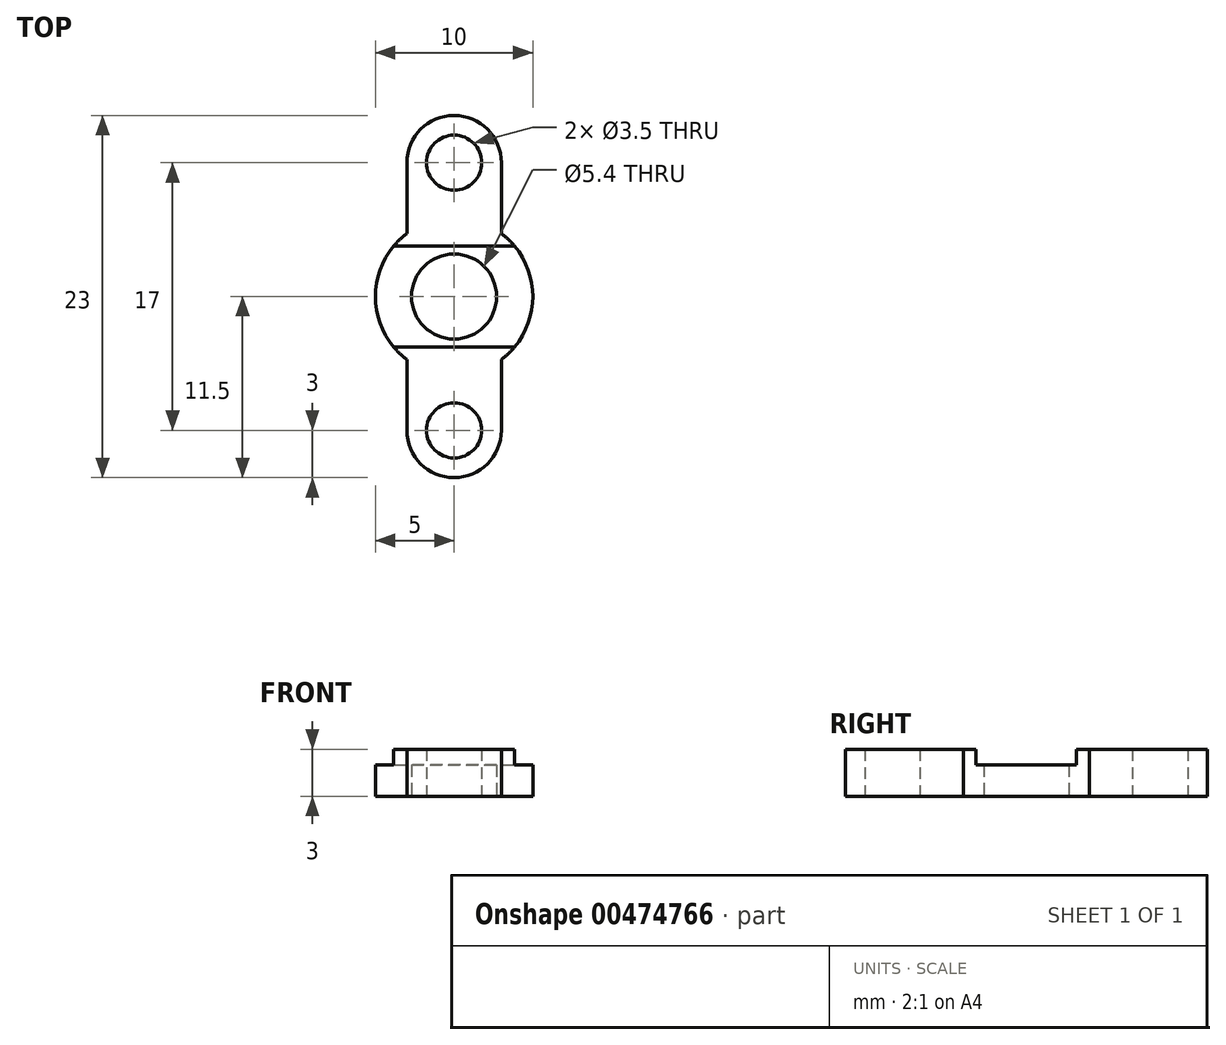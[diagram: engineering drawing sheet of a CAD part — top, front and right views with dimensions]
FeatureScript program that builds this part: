
annotation { "Feature Type Name" : "Feature", "Feature Type Description" : "" }
export const myFeature = defineFeature(function(context is Context, id is Id, definition is map)
    precondition{}
    {
        {
            var Q0;
            Q0=qCreatedBy(makeId("Top.planeOp"),FACE);
            var sketch = newSketch(context, id + "F0", { "sketchPlane" : qUnion([Q0])});
            skLineSegment(sketch, "E0", {"start": v(0, 0) * mm, "end": v(0, 4.5) * mm});
            skLineSegment(sketch, "E1", {"start": v(6, 0) * mm, "end": v(6, 4.5) * mm});
            skArc(sketch, "E2", {"start": v(6, 17) * mm, "mid": v(3, 20) * mm, "end": v(0, 17) * mm});
            skArc(sketch, "E3", {"start": v(0, 0) * mm, "mid": v(3, -3) * mm, "end": v(6, 0) * mm});
            skCircle(sketch, "E4", {"center": v(3, 8.5) * mm, "radius": 2.7 * mm});
            skCircle(sketch, "E5", {"center": v(3, 17) * mm, "radius": 1.75 * mm});
            skCircle(sketch, "E6", {"center": v(3, 0) * mm, "radius": 1.75 * mm});
            skLineSegment(sketch, "E7", {"start": v(3, 17) * mm, "end": v(3, 0) * mm, "construction": true});
            skArc(sketch, "E8", {"start": v(0, 12.5) * mm, "mid": v(-2, 8.5) * mm, "end": v(0, 4.5) * mm});
            skLineSegment(sketch, "E9.trimOffspring", {"start": v(0, 12.5) * mm, "end": v(0, 17) * mm});
            skLineSegment(sketch, "E10.trimOffspring", {"start": v(6, 12.5) * mm, "end": v(6, 17) * mm});
            skArc(sketch, "E11.trimOffspring", {"start": v(6, 4.5) * mm, "mid": v(8, 8.5) * mm, "end": v(6, 12.5) * mm});
            skSolve(sketch);
        }
        {
            var Q0;
            Q0 = qSketchRegion(id + "F0", true);
            extrude(context, id + "F1", {"entities" : qUnion([Q0]), "depth" : 3 * mm, "offsetDistance" : 25 * mm});
        }
        {
            var Q0;
            Q0=makeQuery(id+"F1.opExtrude","CAP_FACE",FACE,{"disambiguationData":[OSD([sQuery(id+"F0.wireOp",EDGE,"E0"),sQuery(id+"F0.wireOp",EDGE,"E1"),sQuery(id+"F0.wireOp",EDGE,"E2"),sQuery(id+"F0.wireOp",EDGE,"E3"),sQuery(id+"F0.wireOp",EDGE,"E4"),sQuery(id+"F0.wireOp",EDGE,"E5"),sQuery(id+"F0.wireOp",EDGE,"E6"),sQuery(id+"F0.wireOp",EDGE,"E8"),sQuery(id+"F0.wireOp",EDGE,"E9.trimOffspring"),sQuery(id+"F0.wireOp",EDGE,"E10.trimOffspring"),sQuery(id+"F0.wireOp",EDGE,"E11.trimOffspring")])],"isStart":false});
            var sketch = newSketch(context, id + "F2", { "sketchPlane" : qUnion([Q0])});
            skLineSegment(sketch, "E12", {"start": v(-0.84, 11.7) * mm, "end": v(6.84, 11.7) * mm});
            skLineSegment(sketch, "E13", {"start": v(-0.84, 5.3) * mm, "end": v(6.84, 5.3) * mm});
            skLineSegment(sketch, "E14", {"start": v(-0.84, 11.7) * mm, "end": v(6.84, 5.3) * mm, "construction": true});
            skLineSegment(sketch, "E15", {"start": v(-0.84, 5.3) * mm, "end": v(6.84, 11.7) * mm, "construction": true});
            skArc(sketch, "E16", {"start": v(-0.84, 11.7) * mm, "mid": v(-2, 8.5) * mm, "end": v(-0.84, 5.3) * mm});
            skArc(sketch, "E17", {"start": v(6.84, 5.3) * mm, "mid": v(8, 8.5) * mm, "end": v(6.84, 11.7) * mm});
            skCircle(sketch, "E18", {"center": v(3, 8.5) * mm, "radius": 2.7 * mm});
            skSolve(sketch);
        }
        {
            var Q0;
            Q0 = qSketchRegion(id + "F2", true);
            extrude(context, id + "F3", {"entities" : qUnion([Q0]), "operationType" : NewBodyOperationType.REMOVE, "oppositeDirection" : true, "depth" : 1 * mm, "offsetDistance" : 25 * mm});
        }
    });
